# Revit family: Diverter_Valve-Whitehall-BestCare-WHDIV
name_source: partatom
category: Plumbing Fixtures
units: mm (PartAtom-declared; Revit-internal decimal feet)

## family parameters
Cut with Voids When Loaded = No
Host = Face
OmniClass Number = 23.65.55.14.17
OmniClass Title = Adjusting/Controlling Valves for Liquid Services
Part Type = Normal
Room Calculation Point = No
Round Connector Dimension = Use Diameter
Shared = Yes

## types (1)
- WHDIV
    ADA Compliant = Yes
    Assembly Code = D2020300
    CW Connection = Yes
    CWFU = 3
    Cold Water Connection Diameter = 1/2"
    Default Elevation = 0"
    Description = BestCare® Ligature-Resistant Diverter Valve
    Finish = Brass-Whitehall-Chrome Plated
    HW Connection = Yes
    HWFU = 3
    Height = 2 3/4"
    Hot Water Connection Diameter = 1/2"
    Installation Type = Wallmount
    Length = 5 1/2"
    Manufacturer = Whitehall
    Material = Brass-Whitehall-Chrome Plated
    Model = WHDIV
    Price = Prices may vary. Please consult Manufacturer Representative for most up-to-date price list.
    Product Documentation Link = https://www.whitehallmfg.com
    Product Page URL = https://www.whitehallmfg.com
    Tempered Water Connection = Yes
    Tempered Water Connection Diameter = 1/2"
    URL = https://www.whitehallmfg.com
    Vent Connection = No
    WFU = 0
    Waste Connection = No

## geometry (parser evidence)
native form markers: Sweep x3
no freeform markers — native parametric forms only
